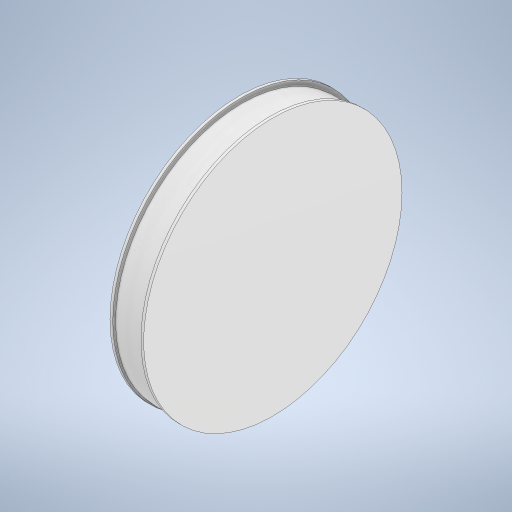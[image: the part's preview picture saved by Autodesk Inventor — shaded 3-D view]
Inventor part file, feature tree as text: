
AUTODESK INVENTOR PART (.ipt)
format: ipt  version: 2023 (Build 270158000, 158)  size: 241,664 bytes
history: native  units: mm
features: extrude x3, sketch x3, other x1
ambient origin geometry x8: Origin, YZ Plane, XZ Plane, XY Plane, X Axis, Y Axis, Z Axis, Center Point
bodies: Body1 (feature_tree)
feature tree (7):
  other  "ソリッド1"
  extrude  "押し出し1"  Depth=90.0mm
  extrude  "押し出し2"  Depth=10.0mm TaperAngle=0.0deg
  extrude  "押し出し3"  Depth=92.0mm
  sketch  "スケッチ1"
  sketch  "スケッチ2"
  sketch  "スケッチ3"
